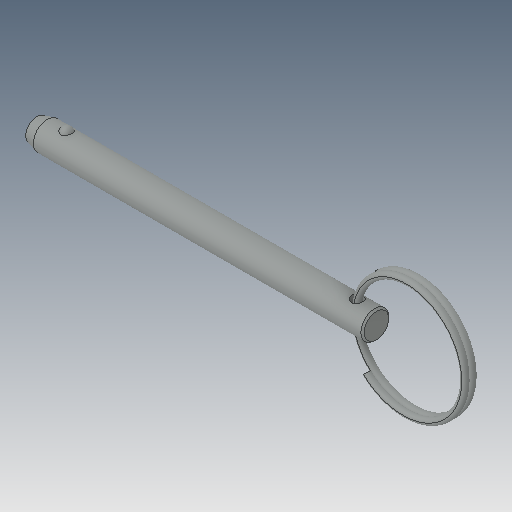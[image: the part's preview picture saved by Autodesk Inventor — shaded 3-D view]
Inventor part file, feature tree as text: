
AUTODESK INVENTOR PART (.ipt)
format: ipt  version: 2023.5 (Build 275446000, 446)  size: 215,552 bytes
history: native  units: in
note: dims shown in document units (in); Inventor stores cm internally (conversion verified against a paired STEP export)
features: revolve x1, other x1, sweep x1
ambient origin geometry x8: Origin, YZ Plane, XZ Plane, XY Plane, X Axis, Y Axis, Z Axis, Center Point
bodies: Solid1 (feature_tree), Solid2 (feature_tree), Solid3 (feature_tree)
feature tree (3):
  revolve  "Revolve2"  [1 undecoded]
  other  "Cut-Revolve2"
  sweep  "Sweep2"
note: 1 required parameter value undecoded (feature->parameter linkage not recoverable at this tier; creation-order binding heuristic only, values carry confidence <= 0.55)
